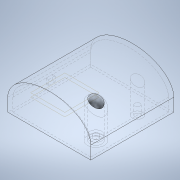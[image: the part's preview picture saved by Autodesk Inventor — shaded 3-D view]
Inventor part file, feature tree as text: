
AUTODESK INVENTOR PART (.ipt)
format: ipt  version: 2021 (Build 250183000, 183)  size: 278,016 bytes
history: native  units: mm
features: sketch x12, extrude x10, plane x2, other x1, shell x1, hole x1, thread x1
ambient origin geometry x8: Origin, YZ Plane, XZ Plane, XY Plane, X Axis, Y Axis, Z Axis, Center Point
bodies: Body1 (feature_tree)
feature tree (28):
  other  "Sólido1"
  sketch  "Boceto1"  dims[d0=2.5mm d2=3.0mm d3=4.0mm]
  extrude  "Extrusión1"  Depth=3.0mm
  shell  "Vaciado1"  Thickness=4.0mm
  plane  "Plano de trabajo2"
  extrude  "Extrusión2"  Depth=2.0mm
  extrude  "Extrusión3"  Depth=64.0mm
  sketch  "Boceto11"  dims[d25=30.0mm d26=0.0mm d27=0.25mm d28=45.0deg]
  sketch  "Boceto12"  dims[d29=2.0mm d30=1.0mm]
  extrude  "Extrusión9"  Depth=40.0mm TaperAngle=0.0deg
  extrude  "Extrusión10"  Depth=2.0mm TaperAngle=0.0deg
  extrude  "Extrusión4"  Depth=10.0mm
  hole  "Agujero1"  [1 undecoded]
  plane  "Plano de trabajo3"
  extrude  "Extrusión6"  Depth=13.0mm
  extrude  "Extrusión8"  Depth=0.25mm
  thread  "Rosca1"  [1 undecoded]
  extrude  "Extrusión13"  Depth=1.0mm
  extrude  "Extrusión14"  TaperAngle=45.0deg  [1 undecoded]
  sketch  "Boceto2"  dims[d4=4.0mm d6=2.0mm]
  sketch  "Boceto3"  dims[d7=30.0mm d8=64.0mm]
  sketch  "Boceto4"  dims[d9=64.0mm d10=40.0mm d11=0.0mm]
  sketch  "Boceto5"  dims[d12=2.0mm d13=20.0mm d14=0.0mm]
  sketch  "Boceto6"  dims[d19=-20.0mm d20=10.0mm]
  sketch  "Boceto8"  dims[d21=16.0mm d22=16.0mm]
  sketch  "Boceto10"  dims[d23=8.0mm d24=13.0mm]
  sketch  "Boceto15"  dims[d31=3.0mm d32=45.0deg]
  sketch  "Boceto16"  dims[d33=2.0mm d34=5.0mm d35=4.0mm d36=0.0mm d37=0.0mm d38=4.0mm d39=7.0mm d40=0.0mm d42=4.0mm d43=4.0mm d44=6.0mm d45=4.0mm d46=2.0mm d47=90.0deg d48=10.0mm d49=0.0mm d55=-3.0mm d56=50.0mm d57=9.0mm d58=0.0mm d59=0.0mm d63=4.0mm d64=2.5mm d65=4.0mm d66=5.0mm d67=0.0mm d68=0.0mm d69=10.0mm d70=10.0mm d71=0.0mm d72=0.0mm d73=64.0mm d74=0.0mm d76=20.0mm d85=2.0mm d86=0.0mm d87=13.0mm d88=1.0mm d89=0.0mm d90=13.0mm d91=9.0mm d92=2.0mm d93=0.0mm d95=20.0mm d96=30.0mm d97=2.0mm]
note: 3 required parameter values undecoded (feature->parameter linkage not recoverable at this tier; creation-order binding heuristic only, values carry confidence <= 0.55)
